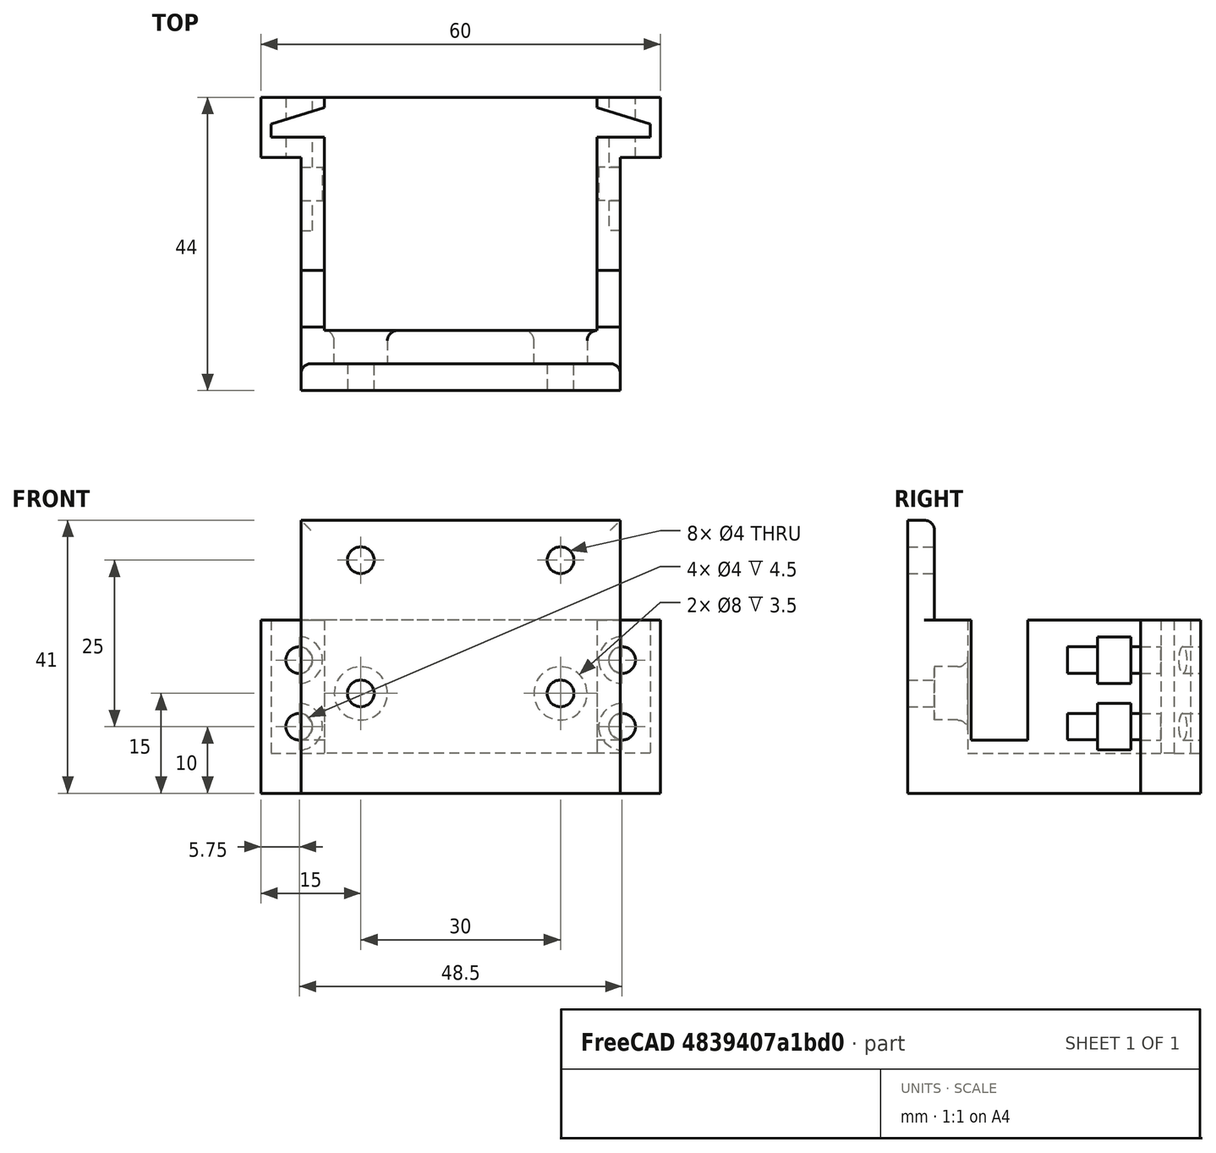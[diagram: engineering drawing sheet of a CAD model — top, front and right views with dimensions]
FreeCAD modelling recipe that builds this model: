
FCSTD DOCUMENT  (FreeCAD 0.18.4R)
Label: Crawler_reset_holder
License: All rights reserved
LicenseURL: http://en.wikipedia.org/wiki/All_rights_reserved
objects: Sketcher::SketchObject×17, TechDraw::DrawViewDimension×13, PartDesign::Pocket×7, TechDraw::DrawViewPart×3, PartDesign::FeatureBase×2, PartDesign::Body×2, Part::Extrusion×1, Spreadsheet::Sheet×1, TechDraw::DrawSVGTemplate×1, TechDraw::DrawViewAnnotation×1, PartDesign::Pad×1, PartDesign::Fillet×1, TechDraw::DrawPage×1
note: 39 computed .brp shape members not serialized (recipe doc carries the construction recipe); baked Part::Feature solids carry a one-line shape summary decoded from their .brp

FEATURE [Sketcher::SketchObject] Sketch
  expr: Constraints[11] = Constraints.dv
  expr: Constraints[5] = Constraints.dv
  expr: Constraints[10] = Constraints.dv
  expr: Constraints[4] = Constraints.dh
  expr: Constraints[3] = Constraints.diameterHole
  sketch-geometry (4):
    g0: Circle CenterX=-33 CenterY=5 CenterZ=0 NormalX=0 NormalY=0 NormalZ=1 AngleXU=0 Radius=4
    g1: Circle CenterX=-33 CenterY=-5 CenterZ=0 NormalX=0 NormalY=0 NormalZ=1 AngleXU=0 Radius=4
    g2: Circle CenterX=15 CenterY=5 CenterZ=0 NormalX=0 NormalY=0 NormalZ=1 AngleXU=0 Radius=4
    g3: Circle CenterX=15 CenterY=-5 CenterZ=0 NormalX=0 NormalY=0 NormalZ=1 AngleXU=0 Radius=4
  constraints (12):
    c: DistanceY(g-1,g0) = 5  'dv'
    c: Radius(g0) = 4  'diameterHole'
    c: DistanceX(g0,g-1) = 33  'dh'
    c: Radius(g1) = 4
    c: DistanceX(g1,g-1) = 33
    c: DistanceY(g1,g-1) = 5
    c: Equal(g0,g2) = 4  'diameterHole'
    c: Equal(g1,g3) = 4
    c: DistanceX(g-1,g2) = 15
    c: DistanceX(g-1,g3) = 15
    c: DistanceY(g3,g-1) = 5
    c: DistanceY(g-1,g2) = 5
FEATURE [Sketcher::SketchObject] Sketch001
  sketch-geometry (51):
    g0: GeomPoint X=-180.398 Y=40.8191 Z=0
    g1: LineSegment StartX=-180.398 StartY=40.8191 StartZ=0 EndX=-141.416 EndY=40.8191 EndZ=0
    g2: ArcOfCircle CenterX=0 CenterY=0 CenterZ=0 NormalX=0 NormalY=0 NormalZ=1 AngleXU=0 Radius=11.54 StartAngle=0 EndAngle=1.04825
    g3: ArcOfCircle CenterX=0 CenterY=0 CenterZ=0 NormalX=0 NormalY=0 NormalZ=1 AngleXU=0 Radius=1.6 StartAngle=0 EndAngle=3.14159
    g4: LineSegment StartX=1.6 StartY=0 StartZ=0 EndX=11.54 EndY=0 EndZ=0
    g5: LineSegment StartX=-1.6 StartY=2e-16 StartZ=0 EndX=-111.4 EndY=0 EndZ=0
    g6: ArcOfCircle CenterX=-139.032 CenterY=0 CenterZ=0 NormalX=0 NormalY=0 NormalZ=1 AngleXU=0 Radius=27.6319 StartAngle=0 EndAngle=1.5708
    g7: LineSegment StartX=-139.032 StartY=27.6319 StartZ=0 EndX=-180.398 EndY=27.6319 EndZ=0
    g8: LineSegment StartX=-180.398 StartY=27.6319 StartZ=0 EndX=-180.398 EndY=40.8191 EndZ=0
    g9: LineSegment [constr] StartX=-139.032 StartY=27.6319 StartZ=0 EndX=-139.032 EndY=0 EndZ=0
    g10: Circle [constr] CenterX=-141.416 CenterY=40.8191 CenterZ=0 NormalX=0 NormalY=0 NormalZ=1 AngleXU=0 Radius=2
    g11: Circle [constr] CenterX=-114.926 CenterY=40.8191 CenterZ=0 NormalX=0 NormalY=0 NormalZ=1 AngleXU=0 Radius=2
    g12: Circle [constr] CenterX=-114.926 CenterY=65 CenterZ=0 NormalX=0 NormalY=0 NormalZ=1 AngleXU=0 Radius=2
    g13: BSplineCurve PolesCount=3 KnotsCount=2 Degree=2 IsPeriodic=0
    g14: GeomPoint [constr] X=-141.416 Y=40.8191 Z=0
    g15: GeomPoint [constr] X=-114.926 Y=65 Z=0
    g16: LineSegment StartX=-114.926 StartY=65 StartZ=0 EndX=-94.9256 EndY=65 EndZ=0
    g17-g21: Circle [constr] x5 (B-spline internal-alignment scaffolding for g22; pole/knot coordinates omitted)
    g22: BSplineCurve PolesCount=5 KnotsCount=3 Degree=3 IsPeriodic=0
    g23: GeomPoint [constr] X=-94.9256 Y=65 Z=0
    g24: GeomPoint [constr] X=-77.0831 Y=42.5915 Z=0
    g25: GeomPoint [constr] X=-59.2405 Y=65 Z=0
    g26: LineSegment StartX=-59.2405 StartY=65 StartZ=0 EndX=-39.2405 EndY=65 EndZ=0
    g27-g30: Circle [constr] x4 (B-spline internal-alignment scaffolding for g31; pole/knot coordinates omitted)
    g31: BSplineCurve PolesCount=4 KnotsCount=2 Degree=3 IsPeriodic=0
    g32: GeomPoint [constr] X=-39.2405 Y=65 Z=0
    g33: GeomPoint [constr] X=5.75948 Y=10 Z=0
    g34: LineSegment [constr] StartX=-94.9256 StartY=46.3979 StartZ=0 EndX=-59.2405 EndY=46.3979 EndZ=0
    g35: LineSegment [constr] StartX=-94.9256 StartY=46.3979 StartZ=0 EndX=-77.0831 EndY=38.7852 EndZ=0
    g36: LineSegment [constr] StartX=-77.0831 StartY=38.7852 StartZ=0 EndX=-59.2405 EndY=46.3979 EndZ=0
    g37: LineSegment [constr] StartX=-141.416 StartY=40.8191 StartZ=0 EndX=-114.926 EndY=40.8191 EndZ=0
    g38: LineSegment [constr] StartX=-39.2405 StartY=65 StartZ=0 EndX=-39.2405 EndY=40 EndZ=0
    g39: LineSegment [constr] StartX=-39.2405 StartY=40 StartZ=0 EndX=-39.2405 EndY=10 EndZ=0
    g40: LineSegment [constr] StartX=-39.2405 StartY=10 StartZ=0 EndX=-24.2405 EndY=10 EndZ=0
    g41: LineSegment [constr] StartX=-59.2405 StartY=46.3979 StartZ=0 EndX=-59.2405 EndY=65 EndZ=0
    g42: LineSegment [constr] StartX=5.75948 StartY=10 StartZ=0 EndX=-24.2405 EndY=10 EndZ=0
    g43: LineSegment [constr] StartX=-114.926 StartY=40.8191 StartZ=0 EndX=-114.926 EndY=65 EndZ=0
    g44: LineSegment [constr] StartX=-94.9256 StartY=65 StartZ=0 EndX=-94.9256 EndY=46.3979 EndZ=0
    g45: Circle CenterX=-45.2405 CenterY=59 CenterZ=0 NormalX=0 NormalY=0 NormalZ=1 AngleXU=0 Radius=2
    g46: Circle CenterX=-45.2405 CenterY=47 CenterZ=0 NormalX=0 NormalY=0 NormalZ=1 AngleXU=0 Radius=2
    g47: LineSegment [constr] StartX=-45.2405 StartY=59 StartZ=0 EndX=-45.2405 EndY=47 EndZ=0
    g48: Circle CenterX=-104.926 CenterY=59 CenterZ=0 NormalX=0 NormalY=0 NormalZ=1 AngleXU=0 Radius=2
    g49: Circle CenterX=-104.926 CenterY=47 CenterZ=0 NormalX=0 NormalY=0 NormalZ=1 AngleXU=0 Radius=2
    g50: LineSegment [constr] StartX=-104.926 StartY=59 StartZ=0 EndX=-104.926 EndY=47 EndZ=0
  constraints (106):
    c: Coincident(g1,g0)
    c: Horizontal(g1)
    c: Coincident(g2,g-1)
    c: PointOnObject(g2,g-1)
    c: PointOnObject(g5,g-1)
    c: Coincident(g3,g-1)
    c: PointOnObject(g3,g-1)
    c: Coincident(g4,g3)
    c: Coincident(g4,g2)
    c: Horizontal(g4)
    c: Coincident(g5,g3)
    c: Radius(g3) = 1.6
    c: PointOnObject(g6,g-1)
    c: Coincident(g6,g5)
    c: Coincident(g7,g6)
    c: Horizontal(g7)
    c: Coincident(g8,g7)
    c: Vertical(g8)
    c: Coincident(g8,g0)
    c: Coincident(g9,g6)
    c: Vertical(g9)
    c: Coincident(g6,g9)
    c: Coincident(g13,g1)
    c: Radius(g10) = 2
    c: Equal(g10,g11)
    c: Equal(g10,g12)
    c: InternalAlignment(g10,g13)
    c: InternalAlignment(g11,g13)
    c: InternalAlignment(g12,g13)
    c: InternalAlignment(g14,g13)
    c: InternalAlignment(g15,g13)
    c: Coincident(g16,g13)
    c: Horizontal(g16)
    c: Coincident(g22,g16)
    c: Radius(g17) = 3
    c: Equal(g17, g18-g21) x4
    c: InternalAlignment(g17-g21 -> g22) x5
    c: InternalAlignment(g23,g22)
    c: InternalAlignment(g24,g22)
    c: InternalAlignment(g25,g22)
    c: Coincident(g26,g22)
    c: Horizontal(g26)
    c: Coincident(g31,g26)
    c: Radius(g27) = 5
    c: Equal(g27,g28)
    c: Equal(g27,g29)
    c: Equal(g27,g30)
    c: InternalAlignment(g27-g30 -> g31) x4
    c: InternalAlignment(g32,g31)
    c: InternalAlignment(g33,g31)
    c: Coincident(g34,g18)
    c: Coincident(g34,g20)
    c: Horizontal(g34)
    c: Coincident(g35,g18)
    c: Coincident(g35,g19)
    c: Coincident(g36,g20)
    c: Equal(g36,g35)
    c: Coincident(g19,g36)
    c: Coincident(g37,g1)
    c: Coincident(g37,g11)
    c: Horizontal(g37)
    c: Coincident(g38,g26)
    c: Coincident(g38,g28)
    c: Vertical(g38)
    c: Coincident(g39,g28)
    c: Vertical(g39)
    c: Coincident(g40,g39)
    c: Coincident(g40,g29)
    c: Horizontal(g40)
    c: DistanceY(g38,g38) = 25
    c: Coincident(g41,g20)
    c: Coincident(g41,g22)
    c: Vertical(g41)
    c: DistanceY(g39,g39) = 30
    c: Coincident(g42,g29)
    c: Horizontal(g42)
    c: DistanceX(g40,g40) = 15
    c: DistanceX(g42,g42) = 30
    c: Coincident(g43,g11)
    c: Coincident(g43,g13)
    c: Vertical(g43)
    c: Coincident(g44,g16)
    c: Coincident(g44,g18)
    c: Vertical(g44)
    c: Radius(g45) = 2
    c: Equal(g45,g46) = 2
    c: Coincident(g47,g45)
    c: Coincident(g47,g46)
    c: Vertical(g47)
    c: DistanceX(g26,g26) = 20
    c: DistanceX(g22,g45) = 14
    c: DistanceY(g45,g22) = 6
    c: DistanceY(g47,g47) = 12
    c: DistanceY(g2,g26) = 65
    c: Equal(g45,g48) = 2
    c: Equal(g48,g49) = 2
    c: Coincident(g50,g48)
    c: Coincident(g50,g49)
    c: Vertical(g50)
    c: Equal(g47,g50) = 12
    c: DistanceX(g16,g16) = 20
    c: DistanceX(g13,g48) = 10
    c: DistanceY(g48,g13) = 6
    c: DistanceY(g2,g16) = 65
    c: DistanceX(g2,g2) = 11.54
    c: DistanceY(g2,g2) = 10
FEATURE [Sketcher::SketchObject] Sketch003  label="ExtrudeToLayOn"
  AttachmentOffset = pos=(0,0,0) rot=(0,0,1;1.5708rad)
  MapMode = 2
  Placement = pos=(0,0,0) rot=(0,0,1;1.5708rad)
  Support = -> [Sketch001]
  expr: Constraints.length = Constraints.hi
  sketch-geometry (10):
    g0: LineSegment StartX=-2.7e-15 StartY=110 StartZ=0 EndX=-2.7e-15 EndY=50 EndZ=0
    g1: LineSegment StartX=-44 StartY=56 StartZ=0 EndX=-44 EndY=104 EndZ=0
    g2: LineSegment StartX=-44 StartY=104 StartZ=0 EndX=-9 EndY=104 EndZ=0
    g3: LineSegment StartX=-44 StartY=56 StartZ=0 EndX=-9 EndY=56 EndZ=0
    g4: LineSegment StartX=-2.7e-15 StartY=50 StartZ=0 EndX=-9 EndY=50 EndZ=0
    g5: LineSegment StartX=-9 StartY=50 StartZ=0 EndX=-9 EndY=56 EndZ=0
    g6: LineSegment StartX=-2.7e-15 StartY=110 StartZ=0 EndX=-9 EndY=110 EndZ=0
    g7: LineSegment StartX=-9 StartY=104 StartZ=0 EndX=-9 EndY=110 EndZ=0
    g8: LineSegment [constr] StartX=-9 StartY=104 StartZ=0 EndX=-9 EndY=80 EndZ=0
    g9: LineSegment [constr] StartX=-9 StartY=80 StartZ=0 EndX=-9 EndY=56 EndZ=0
  constraints (29):
    c: Vertical(g0)
    c: Vertical(g1)
    c: DistanceY(g0,g0) = 60
    c: Coincident(g2,g1)
    c: Horizontal(g2)
    c: DistanceX(g2,g2) = 35  'hi'
    c: Coincident(g3,g1)
    c: Horizontal(g3)
    c: DistanceX(g3,g3) = 35  'length'
    c: Coincident(g4,g0)
    c: Horizontal(g4)
    c: Coincident(g5,g4)
    c: Coincident(g5,g3)
    c: Vertical(g5)
    c: Coincident(g6,g0)
    c: Horizontal(g6)
    c: Vertical(g7)
    c: Coincident(g7,g6)
    c: Coincident(g2,g7)
    c: Equal(g5,g7)
    c: DistanceY(g1,g1) = 48
    c: DistanceX(g4,g0) = 9
    c: DistanceX(g1,g-1) = 44
    c: Coincident(g8,g2)
    c: Vertical(g8)
    c: Coincident(g9,g8)
    c: Coincident(g9,g3)
    c: Equal(g8,g9)
    c: DistanceY(g-1,g8) = 80
FEATURE [Part::Extrusion] Extrude001
  Base = -> Sketch003
  Dir = (0,0,1)
  DirMode = 2
  FaceMakerClass = Part::FaceMakerBullseye
  LengthFwd = 26
  LengthRev = 0
  Placement = pos=(0,0,2) rot=(0,0,1;0rad)
  Solid = true
  Symmetric = false
FEATURE [Sketcher::SketchObject] Sketch004  label="Servo"
  AttachmentOffset = pos=(0,-3,-2) rot=(0,0,1;0rad)
  MapMode = 5
  Placement = pos=(0,-3,26) rot=(0,0,1;0rad)
  Support = -> [Extrude001]
  expr: Constraints[35] = Constraints.strebeH
  sketch-geometry (21):
    g0: LineSegment StartX=-100.5 StartY=4.5 StartZ=0 EndX=-59.5 EndY=4.5 EndZ=0
    g1: LineSegment StartX=-59.5 StartY=-32 StartZ=0 EndX=-100.5 EndY=-32 EndZ=0
    g2: LineSegment [constr] StartX=-59.5 StartY=4.5 StartZ=0 EndX=-59.5 EndY=-1 EndZ=0
    g3: LineSegment [constr] StartX=-59.5 StartY=-1 StartZ=0 EndX=-51.5 EndY=-1 EndZ=0
    g4: LineSegment StartX=-51.5 StartY=-1 StartZ=0 EndX=-51.5 EndY=-3 EndZ=0
    g5: LineSegment StartX=-51.5 StartY=-3 StartZ=0 EndX=-59.5 EndY=-3 EndZ=0
    g6: LineSegment [constr] StartX=-100.5 StartY=4.5 StartZ=0 EndX=-100.5 EndY=-1 EndZ=0
    g7: LineSegment [constr] StartX=-100.5 StartY=-1 StartZ=0 EndX=-108.5 EndY=-1 EndZ=0
    g8: LineSegment StartX=-108.5 StartY=-1 StartZ=0 EndX=-108.5 EndY=-3 EndZ=0
    g9: LineSegment StartX=-108.5 StartY=-3 StartZ=0 EndX=-100.5 EndY=-3 EndZ=0
    g10: GeomPoint X=-80 Y=-3 Z=0
    g11: LineSegment [constr] StartX=-100.5 StartY=-3 StartZ=0 EndX=-80 EndY=-3 EndZ=0
    g12: LineSegment [constr] StartX=-80 StartY=-3 StartZ=0 EndX=-59.5 EndY=-3 EndZ=0
    g13: GeomPoint X=-59.5 Y=1.5 Z=0
    g14: GeomPoint X=-100.5 Y=1.5 Z=0
    g15: LineSegment StartX=-108.5 StartY=-1 StartZ=0 EndX=-100.5 EndY=1.5 EndZ=0
    g16: LineSegment StartX=-100.5 StartY=1.5 StartZ=0 EndX=-100.5 EndY=4.5 EndZ=0
    g17: LineSegment StartX=-51.5 StartY=-1 StartZ=0 EndX=-59.5 EndY=1.5 EndZ=0
    g18: LineSegment StartX=-59.5 StartY=1.5 StartZ=0 EndX=-59.5 EndY=4.5 EndZ=0
    g19: LineSegment StartX=-100.5 StartY=-3 StartZ=0 EndX=-100.5 EndY=-32 EndZ=0
    g20: LineSegment StartX=-59.5 StartY=-32 StartZ=0 EndX=-59.5 EndY=-3 EndZ=0
  constraints (54):
    c: Horizontal(g0)
    c: DistanceX(g0,g0) = 41  'vl'
    c: DistanceY(g1,g0) = 36.5
    c: Coincident(g2,g0)
    c: Vertical(g2)
    c: DistanceY(g2,g2) = 5.5  'vh'
    c: Coincident(g3,g2)
    c: Horizontal(g3)
    c: Coincident(g4,g3)
    c: Vertical(g4)
    c: Coincident(g5,g4)
    c: Horizontal(g5)
    c: DistanceX(g0,g1) = 0
    c: Vertical(g6)
    c: Coincident(g7,g6)
    c: Horizontal(g7)
    c: Coincident(g8,g7)
    c: Vertical(g8)
    c: Coincident(g9,g8)
    c: Horizontal(g9)
    c: Coincident(g6,g0)
    c: DistanceY(g6,g6) = 5.5
    c: DistanceY(g1,g9) = 29
    c: Horizontal(g1)
    c: DistanceX(g1,g1) = 41
    c: DistanceX(g7,g6) = 8
    c: DistanceX(g2,g3) = 8
    c: Coincident(g11,g10)
    c: Horizontal(g11)
    c: Coincident(g12,g10)
    c: Equal(g11,g12)
    c: DistanceX(g10,g-1) = 80  'HvonOrg'
    c: PointOnObject(g13,g2)
    c: DistanceY(g2,g13) = 2.5  'strebeH'
    c: PointOnObject(g14,g6)
    c: DistanceY(g6,g14) = 2.5
    c: Coincident(g15,g7)
    c: Coincident(g15,g14)
    c: Coincident(g16,g14)
    c: Coincident(g16,g0)
    c: Coincident(g17,g3)
    c: Coincident(g17,g13)
    c: Coincident(g18,g13)
    c: Coincident(g18,g0)
    c: Coincident(g19,g9)
    c: Coincident(g19,g1)
    c: Vertical(g19)
    c: Coincident(g20,g1)
    c: Vertical(g20)
    c: Coincident(g5,g20)
    c: Coincident(g5,g12)
    c: Coincident(g9,g11)
    c: Horizontal(g12)
    c: DistanceY(g1,g-1) = 32
FEATURE [PartDesign::FeatureBase] BaseFeature001
  BaseFeature = -> Extrude001
FEATURE [PartDesign::Pocket] Pocket001
  BaseFeature = -> BaseFeature001
  Length = 20
  Length2 = 100
  Profile = -> Sketch004
  Type = 0
FEATURE [Sketcher::SketchObject] Sketch005  label="ServoHoles"
  MapMode = 5
  Placement = pos=(0,-2.4e-15,0) rot=(0,0.707107,0.707107;3.14159rad)
  Support = -> [Pocket001]
  expr: Constraints.height = 5mm + 5mm
  expr: Constraints[14] = Sketch004.Constraints.HvonOrg
  sketch-geometry (7):
    g0: Circle CenterX=55.75 CenterY=20 CenterZ=0 NormalX=0 NormalY=0 NormalZ=1 AngleXU=0 Radius=2
    g1: Circle CenterX=55.75 CenterY=10 CenterZ=0 NormalX=0 NormalY=0 NormalZ=1 AngleXU=0 Radius=2
    g2: Circle CenterX=104.25 CenterY=10 CenterZ=0 NormalX=0 NormalY=0 NormalZ=1 AngleXU=0 Radius=2
    g3: Circle CenterX=104.25 CenterY=20 CenterZ=0 NormalX=0 NormalY=0 NormalZ=1 AngleXU=0 Radius=2
    g4: GeomPoint X=57.75 Y=20 Z=0
    g5: GeomPoint X=102.25 Y=20 Z=0
    g6: GeomPoint X=80 Y=8 Z=0
  constraints (17):
    c: Radius(g0) = 2  'rad'
    c: Equal(g0,g1) = 2  'rad'
    c: DistanceY(g1,g0) = 10
    c: DistanceX(g0,g1) = 0
    c: Equal(g0,g3) = 2  'rad'
    c: Equal(g3,g2) = 2  'rad'
    c: DistanceY(g2,g3) = 10
    c: DistanceX(g3,g2) = 0
    c: DistanceY(g0,g3) = 0
    c: DistanceY(g-1,g1) = 10  'height'
    c: PointOnObject(g4,g0)
    c: PointOnObject(g5,g3)
    c: DistanceY(g4,g0) = 0
    c: DistanceY(g5,g4) = 0
    c: DistanceX(g-1,g6) = 80
    c: DistanceX(g4,g6) = 22.25
    c: DistanceX(g6,g5) = 22.25
FEATURE [PartDesign::Pocket] Pocket002
  BaseFeature = -> Pocket001
  Length = 20
  Length2 = 100
  Profile = -> Sketch005
  Type = 0
FEATURE [PartDesign::Body] Body001
  BaseFeature = -> Extrude001
  Group = -> [BaseFeature001,Sketch004,Pocket001,Sketch005,Pocket002]
  Origin = -> Origin001
  Placement = pos=(0,0,4) rot=(0,0,1;0rad)
  Tip = -> Pocket002
  expr: Placement.Base.y = global.offestSev
FEATURE [Sketcher::SketchObject] Sketch007
  Placement = pos=(2,0,17) rot=(0,0,1;1.5708rad)
  expr: Constraints[28] = Constraints.vh
  expr: Constraints[29] = Constraints.vh2
  sketch-geometry (12):
    g0: LineSegment StartX=1.28047 StartY=41.4016 StartZ=0 EndX=42.2805 EndY=41.4016 EndZ=0
    g1: LineSegment StartX=42.2805 StartY=4.90163 StartZ=0 EndX=1.04145 EndY=4.90163 EndZ=0
    g2: LineSegment StartX=42.2805 StartY=4.90163 StartZ=0 EndX=42.2805 EndY=31.3016 EndZ=0
    g3: LineSegment StartX=42.2805 StartY=41.4016 StartZ=0 EndX=42.2805 EndY=35.4016 EndZ=0
    g4: LineSegment StartX=42.2805 StartY=35.4016 StartZ=0 EndX=48.9967 EndY=35.4016 EndZ=0
    g5: LineSegment StartX=48.9967 StartY=35.4016 StartZ=0 EndX=48.9967 EndY=31.3016 EndZ=0
    g6: LineSegment StartX=48.9967 StartY=31.3016 StartZ=0 EndX=42.2805 EndY=31.3016 EndZ=0
    g7: LineSegment StartX=1.04145 StartY=4.90163 StartZ=0 EndX=1.04145 EndY=31.3016 EndZ=0
    g8: LineSegment StartX=1.28047 StartY=41.4016 StartZ=0 EndX=1.28047 EndY=35.4016 EndZ=0
    g9: LineSegment StartX=1.28047 StartY=35.4016 StartZ=0 EndX=-5.63119 EndY=35.4016 EndZ=0
    g10: LineSegment StartX=-5.63119 StartY=35.4016 StartZ=0 EndX=-5.63119 EndY=31.3016 EndZ=0
    g11: LineSegment StartX=-5.63119 StartY=31.3016 StartZ=0 EndX=1.04145 EndY=31.3016 EndZ=0
  constraints (31):
    c: Horizontal(g0)
    c: DistanceX(g0,g0) = 41  'v'
    c: DistanceY(g1,g0) = 36.5
    c: Coincident(g2,g1)
    c: Vertical(g2)
    c: DistanceY(g2,g2) = 26.4  'vh2'
    c: Coincident(g3,g0)
    c: Vertical(g3)
    c: DistanceY(g3,g3) = 6  'vh'
    c: Coincident(g4,g3)
    c: Horizontal(g4)
    c: Coincident(g5,g4)
    c: Vertical(g5)
    c: Coincident(g6,g5)
    c: Coincident(g6,g2)
    c: Horizontal(g6)
    c: DistanceX(g0,g1) = 0
    c: Vertical(g7)
    c: Vertical(g8)
    c: Coincident(g9,g8)
    c: Horizontal(g9)
    c: Coincident(g10,g9)
    c: Vertical(g10)
    c: Coincident(g11,g10)
    c: Coincident(g11,g7)
    c: Horizontal(g11)
    c: Coincident(g8,g0)
    c: Coincident(g1,g7)
    c: DistanceY(g8,g8) = 6
    c: DistanceY(g7,g7) = 26.4
    c: Horizontal(g1)
FEATURE [Sketcher::SketchObject] Sketch008  label="ServoHole"
  AttachmentOffset = pos=(0,0,4.5) rot=(0,0,1;0rad)
  Placement = pos=(0,0,4.5) rot=(0,0,1;1.5708rad)
  expr: AttachmentOffset.Base.z = global.height
  sketch-geometry (7):
    g0: GeomPoint X=0 Y=19 Z=0
    g1: LineSegment StartX=0 StartY=19 StartZ=0 EndX=2.9 EndY=19 EndZ=0
    g2: LineSegment StartX=2.9 StartY=19 StartZ=0 EndX=2.9 EndY=15.6827 EndZ=0
    g3: ArcOfCircle CenterX=0 CenterY=0 CenterZ=0 NormalX=0 NormalY=0 NormalZ=1 AngleXU=0 Radius=6 StartAngle=0 EndAngle=0.747584
    g4: LineSegment StartX=4.4 StartY=4.07922 StartZ=0 EndX=2.9 EndY=15.6827 EndZ=0
    g5: LineSegment StartX=0 StartY=0 StartZ=0 EndX=6 EndY=0 EndZ=0
    g6: LineSegment StartX=0 StartY=0 StartZ=0 EndX=0 EndY=19 EndZ=0
  constraints (18):
    c: PointOnObject(g0,g-2)
    c: DistanceY(g-1,g0) = 19  'servHoleL'
    c: Coincident(g1,g0)
    c: Horizontal(g1)
    c: DistanceX(g1,g1) = 2.9
    c: Coincident(g2,g1)
    c: Vertical(g2)
    c: Coincident(g3,g-1)
    c: Radius(g3) = 6
    c: PointOnObject(g3,g-1)
    c: DistanceX(g-1,g3) = 4.4
    c: Coincident(g4,g2)
    c: Distance(g4) = 11.7
    c: Coincident(g4,g3)
    c: Coincident(g5,g-1)
    c: Coincident(g5,g3)
    c: Coincident(g6,g-1)
    c: Coincident(g6,g0)
FEATURE [Spreadsheet::Sheet] Spreadsheet  label="global"
  cells = A1=height; B1(height)=4.5; A2=offsetBackwardServo; B2(offestSev)=0
FEATURE [Sketcher::SketchObject] Sketch009  label="servoScrewSmallWhole"
  Placement = pos=(0,0,4.5) rot=(0,0,1;0rad)
  expr: Placement.Base.z = global.height
  sketch-geometry (3):
    g0: GeomPoint X=-19 Y=0 Z=0
    g1: GeomPoint X=-14 Y=0 Z=0
    g2: Circle CenterX=-14 CenterY=0 CenterZ=0 NormalX=0 NormalY=0 NormalZ=1 AngleXU=0 Radius=2
  constraints (5):
    c: PointOnObject(g0,g-1)
    c: DistanceX(g0,g-1) = 19
    c: PointOnObject(g1,g-1)
    c: DistanceX(g0,g1) = 5
    c: Radius(g2) = 2
FEATURE [PartDesign::FeatureBase] BaseFeature002
  BaseFeature = -> Body001
FEATURE [PartDesign::Pocket] Pocket003
  BaseFeature = -> BaseFeature002
  Length = 10
  Length2 = 100
  Profile = -> Sketch009
  Type = 0
FEATURE [Sketcher::SketchObject] Sketch010  label="ServoHoles001"
  AttachmentOffset = pos=(0,0,-10.5) rot=(0,0,1;0rad)
  MapMode = 5
  Placement = pos=(-2.3e-15,-10.5,2.3e-15) rot=(0,0.707107,0.707107;3.14159rad)
  Support = -> [Pocket001]
  expr: Constraints.height = 5mm + 5mm
  expr: Constraints[16] = Constraints.widthDist
  expr: Constraints[14] = Sketch004.Constraints.HvonOrg
  sketch-geometry (7):
    g0: Circle CenterX=55.75 CenterY=20 CenterZ=0 NormalX=0 NormalY=0 NormalZ=1 AngleXU=0 Radius=3.5
    g1: Circle CenterX=55.75 CenterY=10 CenterZ=0 NormalX=0 NormalY=0 NormalZ=1 AngleXU=0 Radius=3.5
    g2: Circle CenterX=104.25 CenterY=10 CenterZ=0 NormalX=0 NormalY=0 NormalZ=1 AngleXU=0 Radius=3.5
    g3: Circle CenterX=104.25 CenterY=20 CenterZ=0 NormalX=0 NormalY=0 NormalZ=1 AngleXU=0 Radius=3.5
    g4: GeomPoint X=59.25 Y=20 Z=0
    g5: GeomPoint X=100.75 Y=20 Z=0
    g6: GeomPoint X=80 Y=8 Z=0
  constraints (17):
    c: Radius(g0) = 3.5  'rad'
    c: Equal(g0,g1) = 2  'rad'
    c: DistanceY(g1,g0) = 10
    c: DistanceX(g0,g1) = 0
    c: Equal(g0,g3) = 2  'rad'
    c: Equal(g3,g2) = 2  'rad'
    c: DistanceY(g2,g3) = 10
    c: DistanceX(g3,g2) = 0
    c: DistanceY(g0,g3) = 0
    c: DistanceY(g-1,g1) = 10  'height'
    c: PointOnObject(g4,g0)
    c: PointOnObject(g5,g3)
    c: DistanceY(g4,g0) = 0
    c: DistanceY(g5,g4) = 0
    c: DistanceX(g-1,g6) = 80
    c: DistanceX(g4,g6) = 20.75  'widthDist'
    c: DistanceX(g6,g5) = 20.75
FEATURE [PartDesign::Pocket] Pocket
  BaseFeature = -> Pocket003
  Length = 5
  Length2 = 100
  Profile = -> Sketch010
  Type = 0
FEATURE [Sketcher::SketchObject] Sketch011  label="CableHole"
  MapMode = 5
  Placement = pos=(-56,1.23e-14,0) rot=(0.57735,0.57735,0.57735;2.0944rad)
  Support = -> [Pocket002]
  sketch-geometry (5):
    g0: GeomPoint X=-5 Y=4 Z=0
    g1: LineSegment StartX=-34.5 StartY=37.056 StartZ=0 EndX=-26 EndY=37.056 EndZ=0
    g2: LineSegment StartX=-26 StartY=37.056 StartZ=0 EndX=-26 EndY=8 EndZ=0
    g3: LineSegment StartX=-26 StartY=8 StartZ=0 EndX=-34.5 EndY=8 EndZ=0
    g4: LineSegment StartX=-34.5 StartY=8 StartZ=0 EndX=-34.5 EndY=37.056 EndZ=0
  constraints (13):
    c: DistanceX(g-1,g0) = -5
    c: Coincident(g1,g2)
    c: Coincident(g2,g3)
    c: Coincident(g3,g4)
    c: Coincident(g4,g1)
    c: Horizontal(g1)
    c: Horizontal(g3)
    c: Vertical(g2)
    c: Vertical(g4)
    c: DistanceX(g2,g0) = 21
    c: DistanceX(g3,g3) = 8.5
    c: DistanceY(g-1,g0) = 4
    c: DistanceY(g0,g2) = 4
FEATURE [PartDesign::Pocket] Pocket004
  BaseFeature = -> Pocket
  Length = 50
  Length2 = 100
  Profile = -> Sketch011
  Type = 0
FEATURE [Sketcher::SketchObject] Sketch012  label="V-strong"
  MapMode = 5
  Placement = pos=(0,0,4.5) rot=(0,0,1;0rad)
  sketch-geometry (7):
    g0: LineSegment StartX=-50.2997 StartY=18.3493 StartZ=0 EndX=-22.213 EndY=3.87885 EndZ=0
    g1: LineSegment StartX=-22.213 StartY=-3.87885 StartZ=0 EndX=-56.0787 EndY=-17.3272 EndZ=0
    g2: LineSegment StartX=-56.0787 StartY=-17.3272 StartZ=0 EndX=-56.0787 EndY=-11.3272 EndZ=0
    g3: LineSegment StartX=-56.0787 StartY=-11.3272 StartZ=0 EndX=-28.213 EndY=0 EndZ=0
    g4: LineSegment StartX=-28.213 StartY=0 StartZ=0 EndX=-50.2997 EndY=12.3493 EndZ=0
    g5: LineSegment StartX=-50.2997 StartY=12.3493 StartZ=0 EndX=-50.2997 EndY=18.3493 EndZ=0
    g6: ArcOfCircle CenterX=-28.213 CenterY=0 CenterZ=0 NormalX=0 NormalY=0 NormalZ=1 AngleXU=0 Radius=7.14461 StartAngle=5.70929 EndAngle=6.85708
  constraints (15):
    c: Coincident(g2,g1)
    c: Vertical(g2)
    c: Coincident(g3,g2)
    c: PointOnObject(g3,g-1)
    c: Coincident(g4,g3)
    c: Coincident(g5,g4)
    c: Coincident(g5,g0)
    c: Vertical(g5)
    c: DistanceY(g2,g2) = 6
    c: DistanceY(g5,g5) = 6
    c: Coincident(g6,g3)
    c: Coincident(g6,g0)
    c: Coincident(g6,g1)
    c: DistanceX(g3,g0) = 6
    c: DistanceX(g3,g1) = 6
FEATURE [Sketcher::SketchObject] Sketch013
  MapMode = 5
  Placement = pos=(0,0,0) rot=(1,0,0;1.5708rad)
  sketch-geometry (3):
    g0: LineSegment StartX=-59 StartY=5 StartZ=0 EndX=-22.1184 EndY=8 EndZ=0
    g1: LineSegment StartX=-22.1184 StartY=8 StartZ=0 EndX=-59 EndY=8 EndZ=0
    g2: LineSegment StartX=-59 StartY=8 StartZ=0 EndX=-59 EndY=5 EndZ=0
  constraints (8):
    c: Coincident(g1,g0)
    c: Horizontal(g1)
    c: Coincident(g2,g1)
    c: Coincident(g2,g0)
    c: Vertical(g2)
    c: DistanceX(g0,g-1) = 59
    c: DistanceY(g-1,g0) = 8
    c: DistanceY(g0,g1) = 3
FEATURE [TechDraw::DrawSVGTemplate] Template
  EditableTexts = Designed_by_Name=Johannes Löwe; Drawing_number=0.0.1; FC-Date=08/08/2021; FC-SC=-; FC-SH=1; FC-Title=RWML Reset Servo Holder; Subtitle=Middle Component; Weight=19.5 g
  Height = 210
  Orientation = 1
  Width = 297
FEATURE [TechDraw::DrawViewAnnotation] Annotation
  Font = osifont
  LineSpace = 80
  LockPosition = false
  MaxWidth = -1
  Rotation = 0
  ScaleType = 0
  Text = NUI Galway
  TextSize = 5
  TextStyle = 2
  X = 202.922
  Y = 35.3083
FEATURE [Sketcher::SketchObject] Sketch014  label="shoe"
  Placement = pos=(0,0,0) rot=(1,0,0;1.5708rad)
  expr: Constraints[6] = global.height
  expr: Constraints[5] = ServoHole.Constraints.servHoleL
  sketch-geometry (2):
    g0: ArcOfCircle CenterX=-19 CenterY=4.5 CenterZ=0 NormalX=0 NormalY=0 NormalZ=1 AngleXU=0 Radius=4 StartAngle=2e-16 EndAngle=3.14159
    g1: LineSegment StartX=-23 StartY=4.5 StartZ=0 EndX=-15 EndY=4.5 EndZ=0
  constraints (7):
    c: Radius(g0) = 4
    c: Coincident(g1,g0)
    c: Coincident(g1,g0)
    c: Horizontal(g1)
    c: PointOnObject(g0,g1)
    c: DistanceX(g0,g-1) = 19
    c: DistanceY(g-1,g0) = 4.5
FEATURE [Sketcher::SketchObject] Sketch015  label="Resetbuffer"
  sketch-geometry (28):
    g0: ArcOfCircle CenterX=0 CenterY=0 CenterZ=0 NormalX=0 NormalY=0 NormalZ=1 AngleXU=0 Radius=11.54 StartAngle=0 EndAngle=1.04825
    g1-g4: Circle [constr] x4 (B-spline internal-alignment scaffolding for g5; pole/knot coordinates omitted)
    g5: BSplineCurve PolesCount=4 KnotsCount=2 Degree=3 IsPeriodic=0
    g6: GeomPoint [constr] X=-39.2405 Y=65 Z=0
    g7: GeomPoint [constr] X=5.75948 Y=10 Z=0
    g8: LineSegment [constr] StartX=-39.2405 StartY=65 StartZ=0 EndX=-39.2405 EndY=40 EndZ=0
    g9: LineSegment [constr] StartX=-39.2405 StartY=40 StartZ=0 EndX=-39.2405 EndY=10 EndZ=0
    g10: LineSegment [constr] StartX=-39.2405 StartY=10 StartZ=0 EndX=-24.2405 EndY=10 EndZ=0
    g11: LineSegment [constr] StartX=5.75948 StartY=10 StartZ=0 EndX=-24.2405 EndY=10 EndZ=0
    g12: LineSegment StartX=-39.2405 StartY=65 StartZ=0 EndX=-29.2405 EndY=65 EndZ=0
    g13: LineSegment StartX=-29.2405 StartY=65 StartZ=0 EndX=0 EndY=65 EndZ=0
    g14: LineSegment StartX=31.54 StartY=0 StartZ=0 EndX=11.54 EndY=0 EndZ=0
    g15: Circle CenterX=-24.2405 CenterY=60 CenterZ=0 NormalX=0 NormalY=0 NormalZ=1 AngleXU=0 Radius=2
    g16: Circle CenterX=-9.24052 CenterY=60 CenterZ=0 NormalX=0 NormalY=0 NormalZ=1 AngleXU=0 Radius=2
    g17: LineSegment [constr] StartX=-24.2405 StartY=60 StartZ=0 EndX=-9.24052 EndY=60 EndZ=0
    g18: Circle CenterX=17.9917 CenterY=18.4952 CenterZ=0 NormalX=0 NormalY=0 NormalZ=1 AngleXU=0 Radius=2
    g19: Circle CenterX=24.54 CenterY=5 CenterZ=0 NormalX=0 NormalY=0 NormalZ=1 AngleXU=0 Radius=2
    g20: LineSegment [constr] StartX=17.9917 StartY=18.4952 StartZ=0 EndX=24.54 EndY=5 EndZ=0
    g21-g24: Circle [constr] x4 (B-spline internal-alignment scaffolding for g25; pole/knot coordinates omitted)
    g25: BSplineCurve PolesCount=4 KnotsCount=2 Degree=3 IsPeriodic=0
    g26: GeomPoint [constr] X=0 Y=65 Z=0
    g27: GeomPoint [constr] X=31.54 Y=0 Z=0
  constraints (60):
    c: PointOnObject(g0,g-1)
    c: Radius(g1) = 5
    c: Equal(g1,g2)
    c: Equal(g1,g3)
    c: Equal(g1,g4)
    c: Coincident(g5,g0)
    c: InternalAlignment(g1-g4 -> g5) x4
    c: InternalAlignment(g6,g5)
    c: InternalAlignment(g7,g5)
    c: Coincident(g8,g2)
    c: Vertical(g8)
    c: Coincident(g9,g2)
    c: Vertical(g9)
    c: Coincident(g10,g9)
    c: Coincident(g10,g3)
    c: Horizontal(g10)
    c: DistanceY(g8,g8) = 25
    c: DistanceY(g9,g9) = 30
    c: Coincident(g11,g0)
    c: Coincident(g11,g3)
    c: Horizontal(g11)
    c: DistanceX(g10,g10) = 15
    c: DistanceX(g11,g11) = 30
    c: DistanceX(g12,g12) = 10
    c: DistanceY(g0,g0) = 10
    c: DistanceX(g0,g0) = 11.54
    c: Coincident(g5,g8)
    c: Coincident(g5,g12)
    c: Horizontal(g12)
    c: Coincident(g13,g12)
    c: PointOnObject(g13,g-2)
    c: Horizontal(g13)
    c: Horizontal(g14)
    c: DistanceX(g14,g14) = 20
    c: Coincident(g14,g0)
    c: Radius(g15) = 2
    c: Radius(g16) = 2
    c: Coincident(g17,g15)
    c: Coincident(g17,g16)
    c: Horizontal(g17)
    c: DistanceY(g15,g5) = 5
    c: DistanceX(g5,g15) = 15
    c: DistanceX(g15,g16) = 15
    c: Radius(g18) = 2
    c: Equal(g18,g19) = 2
    c: Coincident(g20,g18)
    c: Coincident(g20,g19)
    c: DistanceY(g0,g19) = 5
    c: Coincident(g0,g-1)
    c: DistanceX(g0,g19) = 13
    c: Distance(g20) = 15
    c: Coincident(g25,g13)
    c: Radius(g21) = 6
    c: Equal(g21,g22)
    c: Equal(g21,g23)
    c: Equal(g21,g24)
    c: Coincident(g25,g14)
    c: InternalAlignment(g21-g24 -> g25) x4
    c: InternalAlignment(g26,g25)
    c: InternalAlignment(g27,g25)
FEATURE [Sketcher::SketchObject] Sketch016  label="extrude"
  MapMode = 5
  Placement = pos=(0,0,26) rot=(0,0,1;0rad)
  Support = -> [Pocket004]
  sketch-geometry (4):
    g0: LineSegment StartX=-104 StartY=-44 StartZ=0 EndX=-56 EndY=-44 EndZ=0
    g1: LineSegment StartX=-56 StartY=-44 StartZ=0 EndX=-56 EndY=-40 EndZ=0
    g2: LineSegment StartX=-56 StartY=-40 StartZ=0 EndX=-104 EndY=-40 EndZ=0
    g3: LineSegment StartX=-104 StartY=-40 StartZ=0 EndX=-104 EndY=-44 EndZ=0
  constraints (12):
    c: Coincident(g0,g1)
    c: Coincident(g1,g2)
    c: Coincident(g2,g3)
    c: Coincident(g3,g0)
    c: Horizontal(g0)
    c: Horizontal(g2)
    c: Vertical(g1)
    c: Vertical(g3)
    c: DistanceY(g0,g-1) = 44
    c: DistanceY(g1,g1) = 4
    c: DistanceX(g1,g-1) = 56
    c: DistanceX(g2,g2) = 48
FEATURE [PartDesign::Pad] Pad
  BaseFeature = -> Pocket004
  Length = 15
  Length2 = 100
  Profile = -> Sketch016
  Type = 0
FEATURE [Sketcher::SketchObject] Sketch017  label="screwholes"
  MapMode = 5
  Placement = pos=(0,-40,0) rot=(0,0.707107,0.707107;3.14159rad)
  Support = -> [Pad]
  sketch-geometry (7):
    g0: Circle CenterX=65 CenterY=35 CenterZ=0 NormalX=0 NormalY=0 NormalZ=1 AngleXU=0 Radius=2
    g1: Circle CenterX=95 CenterY=35 CenterZ=0 NormalX=0 NormalY=0 NormalZ=1 AngleXU=0 Radius=2
    g2: LineSegment [constr] StartX=65 StartY=35 StartZ=0 EndX=95 EndY=35 EndZ=0
    g3: Circle CenterX=65 CenterY=15 CenterZ=0 NormalX=0 NormalY=0 NormalZ=1 AngleXU=0 Radius=2
    g4: Circle CenterX=95 CenterY=15 CenterZ=0 NormalX=0 NormalY=0 NormalZ=1 AngleXU=0 Radius=2
    g5: LineSegment [constr] StartX=65 StartY=15 StartZ=0 EndX=95 EndY=15 EndZ=0
    g6: LineSegment [constr] StartX=65 StartY=35 StartZ=0 EndX=65 EndY=15 EndZ=0
  constraints (18):
    c: Radius(g0) = 2
    c: DistanceY(g-1,g0) = 35
    c: DistanceX(g-1,g0) = 65
    c: Equal(g0,g1) = 2
    c: Coincident(g2,g0)
    c: Coincident(g2,g1)
    c: Horizontal(g2)
    c: DistanceX(g2,g2) = 30
    c: Equal(g0,g3) = 2
    c: Equal(g3,g4) = 2
    c: Coincident(g5,g3)
    c: Coincident(g5,g4)
    c: Horizontal(g5)
    c: Equal(g2,g5) = 40
    c: Coincident(g6,g0)
    c: Coincident(g6,g3)
    c: Vertical(g6)
    c: DistanceY(g6,g6) = 20
FEATURE [PartDesign::Pocket] Pocket005
  BaseFeature = -> Pad
  Length = 10
  Length2 = 100
  Midplane = true
  Profile = -> Sketch017
  Type = 0
FEATURE [Sketcher::SketchObject] Sketch018  label="Screw-senkungen"
  MapMode = 5
  Placement = pos=(0,-40,0) rot=(0,0.707107,0.707107;3.14159rad)
  Support = -> [Pocket005]
  sketch-geometry (3):
    g0: Circle CenterX=65 CenterY=15 CenterZ=0 NormalX=0 NormalY=0 NormalZ=1 AngleXU=0 Radius=4
    g1: Circle CenterX=95 CenterY=15 CenterZ=0 NormalX=0 NormalY=0 NormalZ=1 AngleXU=0 Radius=4
    g2: LineSegment [constr] StartX=65 StartY=15 StartZ=0 EndX=95 EndY=15 EndZ=0
  constraints (8):
    c: Radius(g0) = 4
    c: Radius(g1) = 4
    c: DistanceY(g-1,g0) = 15
    c: DistanceX(g-1,g0) = 65
    c: Coincident(g2,g0)
    c: Coincident(g2,g1)
    c: Horizontal(g2)
    c: DistanceX(g2,g2) = 30
FEATURE [PartDesign::Pocket] Pocket006
  BaseFeature = -> Pocket005
  Length = 5
  Length2 = 100
  Profile = -> Sketch018
  Reversed = true
  Type = 0
FEATURE [PartDesign::Fillet] Fillet
  Base = -> Pocket006 [Edge217,Edge211,Edge186,Edge156,Edge155]
  BaseFeature = -> Pocket006
  Radius = 1.5
FEATURE [PartDesign::Body] Body002
  BaseFeature = -> Body001
  Group = -> [BaseFeature002,Sketch009,Pocket003,Sketch010,Pocket,Sketch011,Pocket004,Sketch014,Sketch016,Pad,Sketch017,Pocket005,Sketch018,Pocket006,Fillet]
  Origin = -> Origin002
  Tip = -> Fillet
FEATURE [TechDraw::DrawViewPart] View  label="Top"
  CoarseView = false
  Direction = (0,0,1)
  Focus = 100
  HardHidden = false
  IsoCount = 0
  IsoHidden = false
  IsoVisible = true
  LockPosition = false
  Perspective = false
  Rotation = 0
  ScaleType = 1
  SeamHidden = false
  SeamVisible = false
  SmoothHidden = false
  SmoothVisible = true
  Source = -> [Body002]
  X = 211.78
  Y = 99.2682
FEATURE [TechDraw::DrawViewPart] View001  label="Front"
  CoarseView = false
  Direction = (0,1,0)
  Focus = 100
  HardHidden = false
  IsoCount = 0
  IsoHidden = false
  IsoVisible = false
  LockPosition = false
  Perspective = false
  Rotation = 0
  ScaleType = 0
  SeamHidden = false
  SeamVisible = false
  SmoothHidden = false
  SmoothVisible = true
  Source = -> [Body002]
  X = 210.212
  Y = 174.377
FEATURE [TechDraw::DrawViewPart] View002  label="Perspective"
  CoarseView = false
  Direction = (5,5,5)
  Focus = 200
  HardHidden = false
  IsoCount = 0
  IsoHidden = false
  IsoVisible = false
  LockPosition = false
  Perspective = false
  Rotation = 0
  Scale = 1.5
  ScaleType = 0
  SeamHidden = false
  SeamVisible = false
  SmoothHidden = true
  SmoothVisible = true
  Source = -> [Body002]
  X = 70.859
  Y = 132.886
FEATURE [TechDraw::DrawViewDimension] Dimension
  Arbitrary = false
  FormatSpec = %.2f
  LockPosition = false
  MeasureType = 1
  OverTolerance = 0
  References2D = -> [View]
  Rotation = 0
  ScaleType = 0
  Type = 2
  UnderTolerance = 0
  X = -113.183
  Y = -28.0041
FEATURE [TechDraw::DrawViewDimension] Dimension001
  Arbitrary = false
  FormatSpec = %.2f
  LockPosition = false
  MeasureType = 1
  OverTolerance = 0
  References2D = -> [View001]
  Rotation = 0
  ScaleType = 0
  Type = 1
  UnderTolerance = 0
  X = 31.1719
  Y = 20.5356
FEATURE [TechDraw::DrawViewDimension] Dimension002
  Arbitrary = false
  FormatSpec = %.2f
  LockPosition = false
  MeasureType = 1
  OverTolerance = 0
  References2D = -> [View]
  Rotation = 0
  ScaleType = 0
  Type = 2
  UnderTolerance = 0
  X = -69.0862
  Y = -0.822454
FEATURE [TechDraw::DrawViewDimension] Dimension003
  Arbitrary = false
  FormatSpec = %.2f
  LockPosition = false
  MeasureType = 1
  OverTolerance = 0
  References2D = -> [View]
  Rotation = 0
  ScaleType = 0
  Type = 2
  UnderTolerance = 0
  X = -91.294
  Y = -1.64851
FEATURE [TechDraw::DrawViewDimension] Dimension004
  Arbitrary = false
  FormatSpec = %.2f
  LockPosition = false
  MeasureType = 1
  OverTolerance = 0
  References2D = -> [View002]
  Rotation = 0
  ScaleType = 0
  Type = 0
  UnderTolerance = 0
  X = 1.50159
  Y = -39.0413
FEATURE [TechDraw::DrawViewDimension] Dimension008
  Arbitrary = false
  FormatSpec = %.2f
  LockPosition = false
  MeasureType = 1
  OverTolerance = 0
  References2D = -> [View]
  Rotation = 0
  ScaleType = 0
  Type = 2
  UnderTolerance = 0
  X = 35.4282
  Y = -4.84921
FEATURE [TechDraw::DrawViewDimension] Dimension009
  Arbitrary = false
  FormatSpec = %.2f
  LockPosition = false
  MeasureType = 1
  OverTolerance = 0
  References2D = -> [View]
  Rotation = 0
  ScaleType = 0
  Type = 1
  UnderTolerance = 0
  X = 15.1593
  Y = -31.768
FEATURE [TechDraw::DrawViewDimension] Dimension010
  Arbitrary = false
  FormatSpec = %.2f
  LockPosition = false
  MeasureType = 1
  OverTolerance = 0
  References2D = -> [View001]
  Rotation = 0
  ScaleType = 0
  Type = 1
  UnderTolerance = 0
  X = 2.07761
  Y = -39.5468
FEATURE [TechDraw::DrawViewDimension] Dimension011
  Arbitrary = false
  FormatSpec = %.2f
  LockPosition = false
  MeasureType = 1
  OverTolerance = 0
  References2D = -> [View001]
  Rotation = 0
  ScaleType = 0
  Type = 2
  UnderTolerance = 0
  X = -44.0684
  Y = -0.383559
FEATURE [TechDraw::DrawViewDimension] Dimension012
  Arbitrary = false
  FormatSpec = ⌀%.2f
  LockPosition = false
  MeasureType = 1
  OverTolerance = 0
  References2D = -> [View001]
  Rotation = 0
  ScaleType = 0
  Type = 5
  UnderTolerance = 0
  X = 38.1506
  Y = 13.6803
FEATURE [TechDraw::DrawViewDimension] Dimension013
  Arbitrary = false
  FormatSpec = ⌀%.2f
  LockPosition = false
  MeasureType = 1
  OverTolerance = 0
  References2D = -> [View001]
  Rotation = 0
  ScaleType = 0
  Type = 5
  UnderTolerance = 0
  X = 28.0542
  Y = 23.2757
FEATURE [TechDraw::DrawViewDimension] Dimension014
  Arbitrary = false
  FormatSpec = ⌀%.2f
  LockPosition = false
  MeasureType = 1
  OverTolerance = 0
  References2D = -> [View001]
  Rotation = 0
  ScaleType = 0
  Type = 5
  UnderTolerance = 0
  X = 0
  Y = 9.11823
FEATURE [TechDraw::DrawViewDimension] Dimension015
  Arbitrary = false
  FormatSpec = ⌀%.2f
  LockPosition = false
  MeasureType = 1
  OverTolerance = 0
  References2D = -> [View001]
  Rotation = 0
  ScaleType = 0
  Type = 5
  UnderTolerance = 0
  X = -40.5619
  Y = -24.2829
FEATURE [TechDraw::DrawPage] Page
  KeepUpdated = true
  ProjectionType = 0
  Template = -> Template
  Views = -> [View,View001,View002,Dimension,Dimension001,Dimension002,Dimension003,Dimension004,Annotation,Dimension008,Dimension009,Dimension010,Dimension011,Dimension012,Dimension013,Dimension014,Dimension015]
